# Revit family: 1143210_Oventrop_GmbH___Co__KG_Cocon_QTZ_DN32__PN25__IG_Verschraubung_mit_Messventil
name_source: partatom
category: Rohrzubehör
units: mm (PartAtom-declared; Revit-internal decimal feet)

## family parameters
Arbeitsebenenbasiert = Nein
Beim Laden mit Abzugskörper schneiden = Nein
Bemaßung runder Anschluss = Durchmesser verwenden
Gemeinsam genutzt = Nein
Immer vertikal = Ja
Teiletyp = Normal

## types (1)
- Cocon QTZ Ms-Durchflussregler PN25 (600-4800 l/h), DN 32, kvs 0 m3/h
    Baugruppenkennzeichen = ????
    Beschreibung = OVENTROP-Regulierventil "Cocon QTZ" mit Messventilen, DN32, AG/IG, 600-4800 l/h
    Bestellnummer = 1143210
    Datanorm Nummer = 1143210
    EAN / GTIN = 4026755421644
    Garniturvariante/Einbausituation = mit Messventilen
    Gehäuseanschlussart = Außengewinde/Innengewinde (in Flussrichtung)
    Gehäusebauform = Durchgang
    Gehäusewerkstoff = Messing
    Generiert am = 12.12.2022
    Generiert durch = Rubicon Professional Solutions GmbH
    Hersteller = Oventrop GmbH & Co. KG
    Herstellerkurzname = Oventrop
    Kosten = 0 $
    Modell = Cocon QTZ Ms-Durchflussregler PN25 (600-4800 l/h), DN 32
    Name der Richtlinie = Heizungsarmaturen
    Oberfläche = gebürstet
    Produktgruppe = 7
    Quelle = http://www.vdi3805-portal.de
    Revisionsdatum der VDI-Datei = 29.07.2021
    Stand der Richtlinie = 01.02.2003
    TGA-Nr = 0040270000021000000030000000010050000000000000000100000000?????
    Typenbezeichnung (Name) = Cocon QTZ Ms-Durchflussregler PN25 (600-4800 l/h), DN 32, kvs 0 m3/h
    Typenkommentare = Die Daten geben den Stand des eingeblendeten Datums wieder. Fuer Vollstaendigkeit und Richtigkeit kann keine Gewaehr uebernommen  werden!
    URL = http://www.oventrop.de
    VDI3805-Richtlinienblatt = 2
    Vorgabe-Ansicht = 0 mm  [stored 0 ft]
    Web-Adresse = http://www.vdi3805-portal.de
    WebService = https://www.catalogue.bim4hvac.com:443
    XML = <?xml version="1.0"?>
<pData xmlns="http://www.rubicon-professional.de xmlns:xsi="http://www.w3.org filename="PART02_Oventrop.VDI" shortname="Oventrop" manufacturername="Oventrop GmbH  and  Co. KG" tganr="0040270000021000000030000000010050000000000000000100000000?????" language="de-DE"/><REC010 IDX="010" index="2" content="010;2;200302;Oventrop GmbH  and  Co. KG;20210729;http://www.oventrop.de;Die Daten geben den Stand des eingeblendeten Datums wieder. Fuer Vollstaendigkeit und Richtigkeit kann keine Gewaehr uebernommen  werden!;4026755000009;;;1;20210401;DEU;DE;201110;49;21;"><RECORDS_100><REC100 IDX="100" index="4" content="100;4;4;Absperr- und Regelarmaturen;;;20030317;"><RECORDS_110><REC110 IDX="110" index="27" content="110;27;27;Cocon QTZ Ms-Durchflussregler PN25 (600-4800 l/h);030;3;20180517;;3901;"><RECORDS_200><REC200 IDX="200" index="2" content="200;2;Durchgang;"><RECORDS_250><REC250 IDX="250" index="100" content="250;100;mit Messventilen;"/></RECORDS_250></REC200></RECORDS_200><RECORDS_300><REC300 IDX="300" index="3" content="300;3;Aussengewinde/Innengewinde (in Flussrichtung);"/></RECORDS_300><RECORDS_400><REC400 IDX="400" index="1" content="400;1;Messing;"><RECORDS_450><REC450 IDX="450" index="5" content="450;5;gebuerstet;"/></RECORDS_450></REC400></RECORDS_400><RECORDS_700><REC700 IDX="700" index="1" content="700;1;1;7;32;0;120;16;4000;;;;1;;;;Einstellwert;;;;;;;;;;;;;;;;;;;;;;0;;0;"><RECORDS_710_04><REC71004 IDX="710.04" index="1" content="710.04;1;4.8;;4800;1;320;"/><REC71004 IDX="710.04" index="2" content="710.04;2;3.96;;3960;1;300;"/><REC71004 IDX="710.04" index="3" content="710.04;3;3.12;;3120;1;285;"/><REC71004 IDX="710.04" index="4" content="710.04;4;2.28;;2280;1;265;"/><REC71004 IDX="710.04" index="5" content="710.04;5;1.44;;1440;1;250;"/><REC71004 IDX="710.04" index="6" content="710.04;6;0.6;;600;1;230;"/></RECORDS_710_04><RECORDS_720><REC720 IDX="720" index="1" content="720;1;1143210;;2;100;;3;"/><REC720 IDX="720" index="2" content="720;2;1143270;;2;100;;1;"/><REC720 IDX="720" index="3" content="720;3;1149310;;2;100;;2;"/><REC720 IDX="720" index="11" content="720;11;1143610;;2;101;;3;"/><REC720 IDX="720" index="12" content="720;12;1143670;;2;101;;1;"/><REC720 IDX="720" index="13" content="720;13;1147310;;2;101;;2;"/></RECORDS_720></REC700></RECORDS_700><RECORDS_800><REC800 IDX="800" index="2" content="800;2;0040270000021000000030000000010050000000000000000100000000?????;OVENTROP-Regulierventil  ''Cocon QTZ '' mit Messventilen, DN32, AG/IG, 600-4800 l/h;"><RECORDS_810><REC810 IDX="810" index="1" content="810;1;1143210;1143210;;4026755421644;1143210;;;OVENTROP-Regulierventil  ''Cocon QTZ '' mit Messventilen, DN32, AG/IG, 600-4800 l/h;;;;PCE;;NPL;"/></RECORDS_810></REC800></RECORDS_800></REC110></RECORDS_110></REC100></RECORDS_100><RECORDS_960><REC960 IDX="960" index="2401" content="960;2401;1143210;1A;ovb_w1143104_1;jpg;Fotorealistisches Produktbild in Farbe;"/><REC960 IDX="960" index="2402" content="960;2402;1143210;1A;ovb_w1143210-2;png;Fotorealistisches Produktbild in Farbe;"/><REC960 IDX="960" index="2403" content="960;2403;1143210;1A;ovb_w1143210-1;png;Fotorealistisches Produktbild in Farbe;"/><REC960 IDX="960" index="2404" content="960;2404;1143210;1U;ovu_w1143104_5;jpg;Unvermasste Strichzeichnung;"/><REC960 IDX="960" index="2405" content="960;2405;1143210;1A;ovb_w1143104_3;jpg;Fotorealistisches Produktbild in Farbe;"/></RECORDS_960><RECORDS_970><REC970 IDX="970" index="662" content="970;662;Cocon QTZ DN25 /DN32  NEU (RFER);0;QUAD;-63;-31;-78.5;1;0;0;0;1;0;124;67;140.6;0;0;0;0;0;0;0;0;"><RECORDS_970_02><REC97002 IDX="970.02" index="1" content="970.02;1;G;ZYLI;14.5745;0;53.0265;0.258819;0;0.965926;0;1;0;6;15.8;0;0;0;0;0;0;0;0;12;"/><REC97002 IDX="970.02" index="2" content="970.02;2;G;VKNT;11.0157;0;39.745;0.258819;0;0.965926;0;1;0;13.75;16;6;0;0;0;0;0;0;0;12;"/><REC97002 IDX="970.02" index="3" content="970.02;3;G;KEGL;10.4333;0;37.5717;0.258819;0;0.965926;0;1;0;2.25;12;16;0;0;0;0;0;0;0;1;"/><REC97002 IDX="970.02" index="4" content="970.02;4;G;ZYLI;7.8451;0;27.9124;0.258819;0;0.965926;0;1;0;10;10;0;0;0;0;0;0;0;0;1;"/><REC97002 IDX="970.02" index="5" content="970.02;5;G;KEGL;7.004;0;24.7732;0.258819;0;0.965926;0;1;0;3.25;26;24;0;0;0;0;0;0;0;1;"/><REC97002 IDX="970.02" index="6" content="970.02;6;G;ZYLI;-14.4133;0;-55.1572;0.258819;0;0.965926;0;1;0;82.75;26;0;0;0;0;0;0;0;0;1;80;"/><REC97002 IDX="970.02" index="7" content="970.02;7;G;KEGL;-15.4103;0;-58.8784;0.258819;0;0.965926;0;1;0;3.85245;27.25;25.9999;0;0;0;0;0;0;0;15;"/><REC97002 IDX="970.02" index="8" content="970.02;8;G;QUAD;-13.25;24;-61.25;0.258819;0;0.965926;0;1;0;25.875;11.75;6.5;0;0;0;0;0;0;0;1;"/><REC97002 IDX="970.02" index="9" content="970.02;9;G;KEGL;-16.1221;0;-61.5347;0.258819;0;0.965926;0;1;0;2.75;31;27.25;0;0;0;0;0;0;0;12;"/><REC97002 IDX="970.02" index="10" content="970.02;10;G;ZYLI;-18.0632;0;-68.7791;0.258819;0;0.965926;0;1;0;7.5;31;0;0;0;0;0;0;0;0;12;"/><REC97002 IDX="970.02" index="11" content="970.02;11;G;KEGL;-18.8397;0;-71.6769;0.258819;0;0.965926;0;1;0;3;26;31;0;0;0;0;0;0;0;12;"/><REC97002 IDX="970.02" index="12" content="970.02;12;G;ZYLI;26;3;0;0;1;0;-1;0;0;23;9;0;0;0;0;0;0;0;0;1;80;"/><REC97002 IDX="970.02" index="13" content="970.02;13;G;ZYLI;-17;8;25;0;1;0;-1;0;0;18;9;0;0;0;0;0;0;0;0;1;80;"/><REC97002 IDX="970.02" index="80" content="970.02;80;H;ZYLI;-63;0;0;1;0;0;0;1;0;130;19;0;0;0;0;0;0;0;0;0;"/></RECORDS_970_02><RECORDS_970_03><REC97003 IDX="970.03" index="10" content="970.03;10;G;ROTA;4.399913;0;16.42074198;0.258819;0;0.965926;0;1;0;1;0;0;0;0;0;360;400;0;0;1;1000;"/><REC97003 IDX="970.03" index="15" content="970.03;15;G;ZYLI;26;8;0;0;1;0;-1;0;0;18;9;0;0;0;0;0;0;0;0;1;1000;"/><REC97003 IDX="970.03" index="16" content="970.03;16;G;ROTA;-17;2;25;0;1;0;-1;0;0;1;0;0;0;0;0;360;300;0;0;1;1000;"/><REC97003 IDX="970.03" index="20" content="970.03;20;G;TRAN;-10.35273608;32;-38.63703994;0;-1;0;-0.258819;0;-0.965926;0;0;1;7;150;0;0;0;0;0;1;"/><REC97003 IDX="970.03" index="21" content="970.03;21;G;TRAN;-10.35273608;24;-38.63703994;-0.965926;0;0.258819;0.258819;0;0.965926;0;0;1;8;100;0;0;0;0;0;1;"/><REC97003 IDX="970.03" index="22" content="970.03;22;G;ROTA;-10.35273608;32;-38.63703994;-0.965926;0;0.258819;0.258819;0;0.965926;1;0;0;0;0;0;90;100;0;0;1;"/><REC97003 IDX="970.03" index="23" content="970.03;23;G;TRAN;-10.35273608;32;-38.63703994;-0.965926;0;0.258819;0;1;0;0;0;1;19;100;0;0;0;0;0;1;"/><REC97003 IDX="970.03" index="24" content="970.03;24;G;ROTA;-15.27029549;32;-56.98963129;-0.965926;0;0.258819;0;1;0;1;0;0;0;0;0;90;100;0;0;1;"/><REC97003 IDX="970.03" index="25" content="970.03;25;G;TRAN;-15.27029549;32;-56.98963129;-0.965926;0;0.258819;-0.258819;0;-0.965926;0;0;1;2;100;0;0;0;0;0;1;"/><REC97003 IDX="970.03" index="35" content="970.03;35;G;VKNT;10.61155447;0;39.60296596;0.258819;0;0.965926;0;1;0;14;16;8;0;0;0;0;0;0;0;12;"/><REC97003 IDX="970.03" index="36" content="970.03;36;G;RURO;14.2350121;0;53.12592994;0.258819;0;0.965926;0;1;0;3;6;16;0;0;0;0;0;0;0;12;"/><REC97003 IDX="970.03" index="37" content="970.03;37;G;ZYLI;14.2350121;0;53.12592994;0.258819;0;0.965926;0;1;0;5;13;0;0;0;0;0;0;0;0;12;"/><REC97003 IDX="970.03" index="40" content="970.03;40;G;ZYLI;-12.42328328;0;-46.36444796;-0.258819;0;-0.965926;0;1;0;4;25.9;0;0;0;0;0;0;0;0;4;"/><REC97003 IDX="970.03" index="41" content="970.03;41;G;ZYLI;-13.45855689;0;-50.22815195;-0.258819;0;-0.965926;0;1;0;5;26;0;0;0;0;0;0;0;0;15;"/><REC97003 IDX="970.03" index="42" content="970.03;42;G;VKNT;-20.35558933;24.14814985;-50.96829434;-0.237587;0.969256;0.064001;0.246029;-0.003693;0.969256;5;2;4;0;0;0;0;0;0;0;15;"/><REC97003 IDX="970.03" index="43" content="970.03;43;G;VKNT;-21.5435151;28.99442998;-50.64829235;-0.250075;0.965888;0.067253;0.25896;-0.000206;0.965888;1.5;4;4;0;0;0;0;0;0;0;15;"/><REC97003 IDX="970.03" index="44" content="970.03;44;G;KEGL;-14.7526489;0;-55.05778194;-0.258819;0;-0.965926;0;1;0;4;26.2;27;0;0;0;0;0;0;0;12;"/><REC97003 IDX="970.03" index="45" content="970.03;45;G;KEGL;-15.78792251;0;-58.921486;-0.258819;0;-0.965926;0;1;0;3;27;31;0;0;0;0;0;0;0;12;"/><REC97003 IDX="970.03" index="46" content="970.03;46;G;VKNT;-16.56437772;0;-61.81926393;-0.258819;0;-0.965926;0;1;0;7;31;70;0;0;0;0;0;0;0;12;"/><REC97003 IDX="970.03" index="47" content="970.03;47;G;KEGL;-18.37610653;0;-68.58074592;-0.258819;0;-0.965926;0;1;0;3;31;26;0;0;0;0;0;0;0;12;"/><REC97003 IDX="970.03" index="48" content="970.03;48;G;ROTA;-14.7526489;0;-55.05778194;-0.791292;0.573513;0.211989;-0.258787;-0.000016;-0.965934;0;1;0;0;0;0;45;200;0;0;12;"/><REC97003 IDX="970.03" index="100" content="970.03;100;D;STRE;0;0;0;1;0;0;0;1;0;101;-3.5;0;3.5;0;0;0;0;0;0;0;"/><REC97003 IDX="970.03" index="101" content="970.03;101;D;BOGN;0;0;0;1;0;0;0;1;0;100;3.5;0;-3.5;0;3.5;0;0;0;0;0;"/><REC97003 IDX="970.03" index="150" content="970.03;150;D;STRE;0;0;-3.5;1;0;0;0;1;0;151;0;0;0;19;0;0;0;0;0;0;"/><REC97003 IDX="970.03" index="151" content="970.03;151;D;STRE;0;0;-3.5;1;0;0;0;1;0;152;0;19;2;19;0;0;0;0;0;0;"/><REC97003 IDX="970.03" index="152" content="970.03;152;D;STRE;0;0;-3.5;1;0;0;0;1;0;153;2;19;2;15;0;0;0;0;0;0;"/><REC97003 IDX="970.03" index="153" content="970.03;153;D;STRE;0;0;-3.5;1;0;0;0;1;0;154;2;15;5;12;0;0;0;0;0;0;"/><REC97003 IDX="970.03" index="154" content="970.03;154;D;STRE;0;0;-3.5;1;0;0;0;1;0;155;5;12;5;8;0;0;0;0;0;0;"/><REC97003 IDX="970.03" index="155" content="970.03;155;D;STRE;0;0;-3.5;1;0;0;0;1;0;156;5;8;8;8;0;0;0;0;0;0;"/><REC97003 IDX="970.03" index="156" content="970.03;156;D;STRE;0;0;-3.5;1;0;0;0;1;0;157;8;8;8;0;0;0;0;0;0;0;"/><REC97003 IDX="970.03" index="157" content="970.03;157;D;STRE;0;0;-3.5;1;0;0;0;1;0;150;8;0;0;0;0;0;0;0;0;0;"/><REC97003 IDX="970.03" index="200" content="970.03;200;D;STRE;0;0;0;1;0;0;0;1;0;201;0;0;28;0;0;0;0;0;0;0;"/><REC97003 IDX="970.03" index="201" content="970.03;201;D;STRE;0;0;0;1;0;0;0;1;0;202;28;0;31;3;0;0;0;0;0;0;"/><REC97003 IDX="970.03" index="202" content="970.03;202;D;STRE;0;0;0;1;0;0;0;1;0;203;31;3;31;7;0;0;0;0;0;0;"/><REC97003 IDX="970.03" index="203" content="970.03;203;D;STRE;0;0;0;1;0;0;0;1;0;204;31;7;0;7;0;0;0;0;0;0;"/><REC97003 IDX="970.03" index="204" content="970.03;204;D;STRE;0;0;0;1;0;0;0;1;0;200;0;7;0;0;0;0;0;0;0;0;"/><REC97003 IDX="970.03" index="300" content="970.03;300;D;STRE;0;0;0;1;0;0;0;1;0;301;24;9;0;9;0;0;0;0;0;0;"/><REC97003 IDX="970.03" index="301" content="970.03;301;D;BOGN;0;0;0;1;0;0;0;1;0;302;0;9;-5;0;10;4.99433749;0.33647917;0;0;0;"/><REC97003 IDX="970.03" index="302" content="970.03;302;D;STRE;0;0;0;1;0;0;0;1;0;303;-5;0;24;0;0;0;0;0;0;0;"/><REC97003 IDX="970.03" index="303" content="970.03;303;D;STRE;0;0;0;1;0;0;0;1;0;300;24;0;24;9;0;0;0;0;0;0;"/><REC97003 IDX="970.03" index="400" content="970.03;400;D;STRE;0;0;0;1;0;0;0;1;0;401;-65;26;9;26;0;0;0;0;0;0;"/><REC97003 IDX="970.03" index="401" content="970.03;401;D;BOGN;0;0;0;1;0;0;0;1;0;402;12;23;9;26;3;9;23;0;0;0;"/><REC97003 IDX="970.03" index="402" content="970.03;402;D;STRE;0;0;0;1;0;0;0;1;0;403;12;23;12;12;0;0;0;0;0;0;"/><REC97003 IDX="970.03" index="403" content="970.03;403;D;BOGN;0;0;0;1;0;0;0;1;0;404;12;12;14;10;2;14;12;0;0;0;"/><REC97003 IDX="970.03" index="404" content="970.03;404;D;STRE;0;0;0;1;0;0;0;1;0;405;14;10;21;10;0;0;0;0;0;0;"/><REC97003 IDX="970.03" index="405" content="970.03;405;D;BOGN;0;0;0;1;0;0;0;1;0;406;21;10;22;11;2;20.17712434;11.82287566;0;0;0;"/><REC97003 IDX="970.03" index="406" content="970.03;406;D;STRE;0;0;0;1;0;0;0;1;0;407;22;11;23;15;0;0;0;0;0;0;"/><REC97003 IDX="970.03" index="407" content="970.03;407;D;BOGN;0;0;0;1;0;0;0;1;0;408;24;16;23;15;1;24;15;0;0;0;"/><REC97003 IDX="970.03" index="408" content="970.03;408;D;STRE;0;0;0;1;0;0;0;1;0;409;24;16;24;0;0;0;0;0;0;0;"/><REC97003 IDX="970.03" index="409" content="970.03;409;D;STRE;0;0;0;1;0;0;0;1;0;410;24;0;-65;0;0;0;0;0;0;0;"/><REC97003 IDX="970.03" index="410" content="970.03;410;D;STRE;0;0;0;1;0;0;0;1;0;400;-65;0;-65;26;0;0;0;0;0;0;"/><REC97003 IDX="970.03" index="1000" content="970.03;1000;H;ZYLI;-50;0;0;1;0;0;0;1;0;100;18;0;0;0;0;0;0;0;0;0;"/></RECORDS_970_03><RECORDS_970_04><REC97004 IDX="970.04" index="1" content="970.04;1;0.8078;0.6235;0;1;0.9059;0.7765;0.0471;1;0.9294;0.7922;0.0118;1;60;0;0;0;1;"/><REC97004 IDX="970.04" index="4" content="970.04;4;0.8078;0.6235;0;1;0.8;0.6;0.1;1;1;1;1;1;48;0;0;0;1;"/><REC97004 IDX="970.04" index="12" content="970.04;12;0.4353;0.4353;0.4353;1;0.2471;0.2471;0.2471;1;0.6235;0.6235;0.6235;1;50;0;0;0;1;"/><REC97004 IDX="970.04" index="15" content="970.04;15;0.8;0;0;1;1;0;0.2471;1;1;0.4157;0.4157;1;80;0;0;0;1;"/></RECORDS_970_04></REC970><REC970 IDX="970" index="673" content="970;673;CoConDN32 Verschrbg IG (RFER);0;QUAD;-102;-26;-30.0222;1;0;0;0;1;0;165;52;60.0444;0;0;0;0;0;0;0;0;"><RECORDS_970_02><REC97002 IDX="970.02" index="1" content="970.02;1;H;ZYLI;-102;0;0;1;0;0;0;0;1;172.5;17.95;0;0;0;0;0;0;0;0;0;"/><REC97002 IDX="970.02" index="2" content="970.02;2;G;VKNT;-69;0;0;1;0;0;0;0;1;20;26;6;0;0;0;0;0;0;0;1;1;"/><REC97002 IDX="970.02" index="3" content="970.02;3;G;VKNT;39;0;0;1;0;0;0;0;1;24;24;6;0;0;0;0;0;0;0;1;1;"/><REC97002 IDX="970.02" index="4" content="970.02;4;G;ROTA;-102;0;-22;1;0;0;0;0;1;1;0;0;0;22;0;360;100;0;0;1;"/><REC97002 IDX="970.02" index="100" content="970.02;100;D;STRE;0;0;0;1;0;0;0;1;0;101;61;0;61;2;0;0;0;0;0;0;"/><REC97002 IDX="970.02" index="101" content="970.02;101;D;STRE;0;0;0;1;0;0;0;1;0;102;139;2.00001;61;2;0;0;0;0;0;0;"/><REC97002 IDX="970.02" index="102" content="970.02;102;D;STRE;0;0;0;1;0;0;0;1;0;103;141;0;139;2.00001;0;0;0;0;0;0;"/><REC97002 IDX="970.02" index="103" content="970.02;103;D;STRE;0;0;0;1;0;0;0;1;0;104;141;0;141;4;0;0;0;0;0;0;"/><REC97002 IDX="970.02" index="104" content="970.02;104;D;STRE;0;0;0;1;0;0;0;1;0;105;137;4;141;4;0;0;0;0;0;0;"/><REC97002 IDX="970.02" index="105" content="970.02;105;D;STRE;0;0;0;1;0;0;0;1;0;106;137;4.05;137;4;0;0;0;0;0;0;"/><REC97002 IDX="970.02" index="106" content="970.02;106;D;STRE;0;0;0;1;0;0;0;1;0;107;137;4.05;0;4.05;0;0;0;0;0;0;"/><REC97002 IDX="970.02" index="107" content="970.02;107;D;STRE;0;0;0;1;0;0;0;1;0;108;0;2.8;0;4.05;0;0;0;0;0;0;"/><REC97002 IDX="970.02" index="108" content="970.02;108;D;STRE;0;0;0;1;0;0;0;1;0;109;0;2.8;1;1.8;0;0;0;0;0;0;"/><REC97002 IDX="970.02" index="109" content="970.02;109;D;STRE;0;0;0;1;0;0;0;1;0;110;1;1.8;19;0.700001;0;0;0;0;0;0;"/><REC97002 IDX="970.02" index="110" content="970.02;110;D;STRE;0;0;0;1;0;0;0;1;0;111;19;0.700001;36.25;0.700005;0;0;0;0;0;0;"/><REC97002 IDX="970.02" index="111" content="970.02;111;D;STRE;0;0;0;1;0;0;0;1;0;112;36.25;0.700005;53;0;0;0;0;0;0;0;"/><REC97002 IDX="970.02" index="112" content="970.02;112;D;STRE;0;0;0;1;0;0;0;1;0;100;53;0;61;0;0;0;0;0;0;0;"/></RECORDS_970_02><RECORDS_970_03><REC97003 IDX="970.03" index="1" content="970.03;1;G;ROTA;-68;21.2;0;-1;0;0;0;1;0;1;0;0;0;-21.2;0;360;90;0;0;4;"/><REC97003 IDX="970.03" index="2" content="970.03;2;G;VKNT;-69;0;0;1;0;0;0;0.866025;0.5;20;26;6;0;0;0;0;0;0;0;1;1000;"/><REC97003 IDX="970.03" index="3" content="970.03;3;G;RURO;-49;0;0;1;0;0;0;1;0;3;8;25;0;0;0;0;0;0;0;1;"/><REC97003 IDX="970.03" index="4" content="970.03;4;G;RURO;-62;0;0;1;0;0;0;1;0;2;50;21.9;0;0;0;0;0;0;0;1;"/><REC97003 IDX="970.03" index="7" content="970.03;7;G;VKNT;63;0;0;-1;0;0;0;0.866025;-0.5;24;24;6;0;0;0;0;0;0;0;1;1010;"/><REC97003 IDX="970.03" index="8" content="970.03;8;G;RURR;39;0;0;-1;0;0;0;1;0;2;4;24;20;20;0;0;0;0;0;1;"/><REC97003 IDX="970.03" index="9" content="970.03;9;G;RURO;35;0;0;-1;0;0;0;1;0;2;19;20;0;0;0;0;0;0;0;1;"/><REC97003 IDX="970.03" index="90" content="970.03;90;D;STRE;0;0;0;1;0;0;0;1;0;91;0;0;15;0;0;0;0;0;0;0;"/><REC97003 IDX="970.03" index="91" content="970.03;91;D;STRE;0;0;0;1;0;0;0;1;0;92;15;0;33;-1;0;0;0;0;0;0;"/><REC97003 IDX="970.03" index="92" content="970.03;92;D;STRE;0;0;0;1;0;0;0;1;0;93;33;-1;34;-2;0;0;0;0;0;0;"/><REC97003 IDX="970.03" index="93" content="970.03;93;D;STRE;0;0;0;1;0;0;0;1;0;94;34;-2;34;-3;0;0;0;0;0;0;"/><REC97003 IDX="970.03" index="94" content="970.03;94;D;STRE;0;0;0;1;0;0;0;1;0;95;34;-3;0;-3;0;0;0;0;0;0;"/><REC97003 IDX="970.03" index="95" content="970.03;95;D;STRE;0;0;0;1;0;0;0;1;0;90;0;-3;0;0;0;0;0;0;0;0;"/><REC97003 IDX="970.03" index="1000" content="970.03;1000;H;ZYLI;-70;0;0;1;0;0;0;1;0;30;18;0;0;0;0;0;0;0;0;0;"/><REC97003 IDX="970.03" index="1010" content="970.03;1010;H;ZYLI;35;0;0;1;0;0;0;1;0;30;21;0;0;0;0;0;0;0;0;0;"/></RECORDS_970_03><RECORDS_970_04><REC97004 IDX="970.04" index="1" content="970.04;1;0.8078;0.6235;0;1;0.9059;0.7765;0.0471;1;0.9294;0.7922;0.0118;1;60;0;0;0;1;"/><REC97004 IDX="970.04" index="4" content="970.04;4;0.8078;0.6235;0;1;0.8;0.6;0.1;1;1;1;1;1;48;0;0;0;1;"/></RECORDS_970_04></REC970><REC970 IDX="970" index="154" content="970;154;Messfuehler, classic, Messing NEU blau (REFR);0;QUAD;-9.2376;0;-14.5;1;0;0;0;1;0;18.4752;38.05;23.5;0;0;0;0;0;0;0;0;"><RECORDS_970_02><REC97002 IDX="970.02" index="1" content="970.02;1;D;STRE;0;0;0;1;0;0;0;1;0;2;1.25;3.5;1.25;1;0;0;0;0;0;0;"/><REC97002 IDX="970.02" index="2" content="970.02;2;D;STRE;0;0;0;1;0;0;0;1;0;3;1.25;1;0;0;0;0;0;0;0;0;"/><REC97002 IDX="970.02" index="3" content="970.02;3;D;STRE;0;0;0;1;0;0;0;1;0;4;0;0;8.75;0;0;0;0;0;0;0;"/><REC97002 IDX="970.02" index="4" content="970.02;4;D;STRE;0;0;0;1;0;0;0;1;0;5;8.75;38.05;8.75;0;0;0;0;0;0;0;"/><REC97002 IDX="970.02" index="5" content="970.02;5;D;STRE;0;0;0;1;0;0;0;1;0;6;8.75;38.05;4.5;38.05;0;0;0;0;0;0;"/><REC97002 IDX="970.02" index="6" content="970.02;6;D;STRE;0;0;0;1;0;0;0;1;0;7;4.5;38.05;3.5;37.25;0;0;0;0;0;0;"/><REC97002 IDX="970.02" index="7" content="970.02;7;D;STRE;0;0;0;1;0;0;0;1;0;8;3.5;37.25;3.5;32.75;0;0;0;0;0;0;"/><REC97002 IDX="970.02" index="8" content="970.02;8;D;STRE;0;0;0;1;0;0;0;1;0;9;3.5;32.75;4.25;32.75;0;0;0;0;0;0;"/><REC97002 IDX="970.02" index="9" content="970.02;9;D;STRE;0;0;0;1;0;0;0;1;0;10;4.25;32.75;4.25;30.75;0;0;0;0;0;0;"/><REC97002 IDX="970.02" index="10" content="970.02;10;D;STRE;0;0;0;1;0;0;0;1;0;11;2.25;30.75;4.25;30.75;0;0;0;0;0;0;"/><REC97002 IDX="970.02" index="11" content="970.02;11;D;STRE;0;0;0;1;0;0;0;1;0;12;2.25;30.75;2.25;29.75;0;0;0;0;0;0;"/><REC97002 IDX="970.02" index="12" content="970.02;12;D;STRE;0;0;0;1;0;0;0;1;0;13;2.25;29.75;4.75;29.75;0;0;0;0;0;0;"/><REC97002 IDX="970.02" index="13" content="970.02;13;D;STRE;0;0;0;1;0;0;0;1;0;14;4.75;29.75;4.75;27.75;0;0;0;0;0;0;"/><REC97002 IDX="970.02" index="14" content="970.02;14;D;STRE;0;0;0;1;0;0;0;1;0;15;4.75;27.75;1.5;27.75;0;0;0;0;0;0;"/><REC97002 IDX="970.02" index="15" content="970.02;15;D;STRE;0;0;0;1;0;0;0;1;0;16;1.5;27.75;0.75;27;0;0;0;0;0;0;"/><REC97002 IDX="970.02" index="16" content="970.02;16;D;STRE;0;0;0;1;0;0;0;1;0;17;0.75;27;0.75;14.5;0;0;0;0;0;0;"/><REC97002 IDX="970.02" index="17" content="970.02;17;D;STRE;0;0;0;1;0;0;0;1;0;18;0.75;14.5;4.13;14.5;0;0;0;0;0;0;"/><REC97002 IDX="970.02" index="18" content="970.02;18;D;STRE;0;0;0;1;0;0;0;1;0;19;4.13;14.5;4.13;3.5;0;0;0;0;0;0;"/><REC97002 IDX="970.02" index="19" content="970.02;19;D;STRE;0;0;0;1;0;0;0;1;0;1;4.13;3.5;1.25;3.5;0;0;0;0;0;0;"/><REC97002 IDX="970.02" index="20" content="970.02;20;G;ROTA;-8.7496;0;0;1;0;0;0;1;0;0;1;0;8.7496;0;0;360;1;0;0;1;"/><REC97002 IDX="970.02" index="21" content="970.02;21;G;VKNT;0;3.5;0;0;1;0;-1;0;0;11;8;6;0;0;0;0;0;0;0;1;"/><REC97002 IDX="970.02" index="22" content="970.02;22;D;BOGN;0;0;0;1;0;0;0;1;0;23;13;6.43774;5;6.43774;9;9;14.5;0;0;0;"/><REC97002 IDX="970.02" index="23" content="970.02;23;D;STRE;0;0;0;1;0;0;0;1;0;24;5;6.43774;5;0;0;0;0;0;0;0;"/><REC97002 IDX="970.02" index="24" content="970.02;24;D;STRE;0;0;0;1;0;0;0;1;0;25;5;0;13;0;0;0;0;0;0;0;"/><REC97002 IDX="970.02" index="25" content="970.02;25;D;STRE;0;0;0;1;0;0;0;1;0;22;13;6.43774;13;0;0;0;0;0;0;0;"/><REC97002 IDX="970.02" index="26" content="970.02;26;G;TRAN;-9;29.75;-14.5;1;0;0;0;0;1;0;0;1;2;22;0;0;0;0;0;22;"/></RECORDS_970_02><RECORDS_970_03><REC97003 IDX="970.03" index="1" content="970.03;1;D;BOGN;0;0;0;1;0;0;0;1;0;2;13;6.43774;5;6.43774;9;9;14.5;0;0;0;"/><REC97003 IDX="970.03" index="2" content="970.03;2;D;STRE;0;0;0;1;0;0;0;1;0;3;5;6.43774;5;0;0;0;0;0;0;0;"/><REC97003 IDX="970.03" index="3" content="970.03;3;D;STRE;0;0;0;1;0;0;0;1;0;4;5;0;13;0;0;0;0;0;0;0;"/><REC97003 IDX="970.03" index="4" content="970.03;4;D;STRE;0;0;0;1;0;0;0;1;0;1;13;6.43774;13;0;0;0;0;0;0;0;"/><REC97003 IDX="970.03" index="5" content="970.03;5;G;TRAN;-9;29.75;-14.5;1;0;0;0;0;1;0;0;1;2;1;0;0;0;0;0;22;"/><REC97003 IDX="970.03" index="6" content="970.03;6;G;ZYLI;0;27.75;0;0;1;0;-1;0;0;2;4.5;0;0;0;0;0;0;0;0;4;"/><REC97003 IDX="970.03" index="7" content="970.03;7;G;KEGL;0;37.25;0;0;1;0;-1;0;0;0.8;6;5;0;0;0;0;0;0;0;4;"/><REC97003 IDX="970.03" index="8" content="970.03;8;G;VKNT;0;32.75;0;0;1;0;-1;0;0;4.5;6;24;0;0;0;0;0;0;0;4;"/><REC97003 IDX="970.03" index="9" content="970.03;9;G;ZYLI;0;30.75;0;0;1;0;-1;0;0;2;4.5;0;0;0;0;0;0;0;0;4;"/><REC97003 IDX="970.03" index="10" content="970.03;10;G;ZYLI;0;29.75;0;0;1;0;-1;0;0;1;6.5;0;0;0;0;0;0;0;0;4;"/><REC97003 IDX="970.03" index="11" content="970.03;11;G;KEGL;0;27;0;0;1;0;-1;0;0;0.75;8.75;8;0;0;0;0;0;0;0;4;"/><REC97003 IDX="970.03" index="12" content="970.03;12;G;ZYLI;0;14.5;0;0;1;0;-1;0;0;12.5;8.75;0;0;0;0;0;0;0;0;4;"/><REC97003 IDX="970.03" index="13" content="970.03;13;G;VKNT;0;3.5;0;0;1;0;-1;0;0;11;8;6;0;0;0;0;0;0;0;4;"/><REC97003 IDX="970.03" index="14" content="970.03;14;G;ZYLI;0;1;0;0;1;0;-1;0;0;3;8.25;0;0;0;0;0;0;0;0;4;"/><REC97003 IDX="970.03" index="15" content="970.03;15;G;KEGL;0;0;0;0;1;0;-1;0;0;1;8.75;8;0;0;0;0;0;0;0;4;"/></RECORDS_970_03><RECORDS_970_04><REC97004 IDX="970.04" index="1" content="970.04;1;0.8078;0.6235;0;1;0.9059;0.7765;0.0471;1;0.9294;0.7922;0.0118;1;60;0;0;0;1;"/><REC97004 IDX="970.04" index="4" content="970.04;4;0.8078;0.6235;0;1;0.8;0.6;0.1;1;1;1;1;1;48;0;0;0;1;"/><REC97004 IDX="970.04" index="22" content="970.04;22;0;0.502;1;1;0.4;0.7;0.7;1;0.3;0.3;0.3;1;16;0;0;0;1;"/></RECORDS_970_04></REC970><REC970 IDX="970" index="153" content="970;153;Messfuehler, classic, Messing NEU rot (REFR);0;QUAD;-9.2376;0;-14.5;1;0;0;0;1;0;18.4752;38.05;23.5;0;0;0;0;0;0;0;0;"><RECORDS_970_02><REC97002 IDX="970.02" index="1" content="970.02;1;D;STRE;0;0;0;1;0;0;0;1;0;2;1.25;3.5;1.25;1;0;0;0;0;0;0;"/><REC97002 IDX="970.02" index="2" content="970.02;2;D;STRE;0;0;0;1;0;0;0;1;0;3;1.25;1;0;0;0;0;0;0;0;0;"/><REC97002 IDX="970.02" index="3" content="970.02;3;D;STRE;0;0;0;1;0;0;0;1;0;4;0;0;8.75;0;0;0;0;0;0;0;"/><REC97002 IDX="970.02" index="4" content="970.02;4;D;STRE;0;0;0;1;0;0;0;1;0;5;8.75;38.05;8.75;0;0;0;0;0;0;0;"/><REC97002 IDX="970.02" index="5" content="970.02;5;D;STRE;0;0;0;1;0;0;0;1;0;6;8.75;38.05;4.5;38.05;0;0;0;0;0;0;"/><REC97002 IDX="970.02" index="6" content="970.02;6;D;STRE;0;0;0;1;0;0;0;1;0;7;4.5;38.05;3.5;37.25;0;0;0;0;0;0;"/><REC97002 IDX="970.02" index="7" content="970.02;7;D;STRE;0;0;0;1;0;0;0;1;0;8;3.5;37.25;3.5;32.75;0;0;0;0;0;0;"/><REC97002 IDX="970.02" index="8" content="970.02;8;D;STRE;0;0;0;1;0;0;0;1;0;9;3.5;32.75;4.25;32.75;0;0;0;0;0;0;"/><REC97002 IDX="970.02" index="9" content="970.02;9;D;STRE;0;0;0;1;0;0;0;1;0;10;4.25;32.75;4.25;30.75;0;0;0;0;0;0;"/><REC97002 IDX="970.02" index="10" content="970.02;10;D;STRE;0;0;0;1;0;0;0;1;0;11;2.25;30.75;4.25;30.75;0;0;0;0;0;0;"/><REC97002 IDX="970.02" index="11" content="970.02;11;D;STRE;0;0;0;1;0;0;0;1;0;12;2.25;30.75;2.25;29.75;0;0;0;0;0;0;"/><REC97002 IDX="970.02" index="12" content="970.02;12;D;STRE;0;0;0;1;0;0;0;1;0;13;2.25;29.75;4.75;29.75;0;0;0;0;0;0;"/><REC97002 IDX="970.02" index="13" content="970.02;13;D;STRE;0;0;0;1;0;0;0;1;0;14;4.75;29.75;4.75;27.75;0;0;0;0;0;0;"/><REC97002 IDX="970.02" index="14" content="970.02;14;D;STRE;0;0;0;1;0;0;0;1;0;15;4.75;27.75;1.5;27.75;0;0;0;0;0;0;"/><REC97002 IDX="970.02" index="15" content="970.02;15;D;STRE;0;0;0;1;0;0;0;1;0;16;1.5;27.75;0.75;27;0;0;0;0;0;0;"/><REC97002 IDX="970.02" index="16" content="970.02;16;D;STRE;0;0;0;1;0;0;0;1;0;17;0.75;27;0.75;14.5;0;0;0;0;0;0;"/><REC97002 IDX="970.02" index="17" content="970.02;17;D;STRE;0;0;0;1;0;0;0;1;0;18;0.75;14.5;4.13;14.5;0;0;0;0;0;0;"/><REC97002 IDX="970.02" index="18" content="970.02;18;D;STRE;0;0;0;1;0;0;0;1;0;19;4.13;14.5;4.13;3.5;0;0;0;0;0;0;"/><REC97002 IDX="970.02" index="19" content="970.02;19;D;STRE;0;0;0;1;0;0;0;1;0;1;4.13;3.5;1.25;3.5;0;0;0;0;0;0;"/><REC97002 IDX="970.02" index="20" content="970.02;20;G;ROTA;-8.7496;0;0;1;0;0;0;1;0;0;1;0;8.7496;0;0;360;1;0;0;1;"/><REC97002 IDX="970.02" index="21" content="970.02;21;G;VKNT;0;3.5;0;0;1;0;-1;0;0;11;8;6;0;0;0;0;0;0;0;1;"/><REC97002 IDX="970.02" index="22" content="970.02;22;D;BOGN;0;0;0;1;0;0;0;1;0;23;13;6.43774;5;6.43774;9;9;14.5;0;0;0;"/><REC97002 IDX="970.02" index="23" content="970.02;23;D;STRE;0;0;0;1;0;0;0;1;0;24;5;6.43774;5;0;0;0;0;0;0;0;"/><REC97002 IDX="970.02" index="24" content="970.02;24;D;STRE;0;0;0;1;0;0;0;1;0;25;5;0;13;0;0;0;0;0;0;0;"/><REC97002 IDX="970.02" index="25" content="970.02;25;D;STRE;0;0;0;1;0;0;0;1;0;22;13;6.43774;13;0;0;0;0;0;0;0;"/><REC97002 IDX="970.02" index="26" content="970.02;26;G;TRAN;-9;29.75;-14.5;1;0;0;0;0;1;0;0;1;2;22;0;0;0;0;0;15;"/></RECORDS_970_02><RECORDS_970_03><REC97003 IDX="970.03" index="1" content="970.03;1;D;BOGN;0;0;0;1;0;0;0;1;0;2;13;6.43774;5;6.43774;9;9;14.5;0;0;0;"/><REC97003 IDX="970.03" index="2" content="970.03;2;D;STRE;0;0;0;1;0;0;0;1;0;3;5;6.43774;5;0;0;0;0;0;0;0;"/><REC97003 IDX="970.03" index="3" content="970.03;3;D;STRE;0;0;0;1;0;0;0;1;0;4;5;0;13;0;0;0;0;0;0;0;"/><REC97003 IDX="970.03" index="4" content="970.03;4;D;STRE;0;0;0;1;0;0;0;1;0;1;13;6.43774;13;0;0;0;0;0;0;0;"/><REC97003 IDX="970.03" index="5" content="970.03;5;G;TRAN;-9;29.75;-14.5;1;0;0;0;0;1;0;0;1;2;1;0;0;0;0;0;15;"/><REC97003 IDX="970.03" index="6" content="970.03;6;G;ZYLI;0;27.75;0;0;1;0;-1;0;0;2;4.5;0;0;0;0;0;0;0;0;4;"/><REC97003 IDX="970.03" index="7" content="970.03;7;G;KEGL;0;37.25;0;0;1;0;-1;0;0;0.8;6;5;0;0;0;0;0;0;0;4;"/><REC97003 IDX="970.03" index="8" content="970.03;8;G;VKNT;0;32.75;0;0;1;0;-1;0;0;4.5;6;24;0;0;0;0;0;0;0;4;"/><REC97003 IDX="970.03" index="9" content="970.03;9;G;ZYLI;0;30.75;0;0;1;0;-1;0;0;2;4.5;0;0;0;0;0;0;0;0;4;"/><REC97003 IDX="970.03" index="10" content="970.03;10;G;ZYLI;0;29.75;0;0;1;0;-1;0;0;1;6.5;0;0;0;0;0;0;0;0;4;"/><REC97003 IDX="970.03" index="11" content="970.03;11;G;KEGL;0;27;0;0;1;0;-1;0;0;0.75;8.75;8;0;0;0;0;0;0;0;4;"/><REC97003 IDX="970.03" index="12" content="970.03;12;G;ZYLI;0;14.5;0;0;1;0;-1;0;0;12.5;8.75;0;0;0;0;0;0;0;0;4;"/><REC97003 IDX="970.03" index="13" content="970.03;13;G;VKNT;0;3.5;0;0;1;0;-1;0;0;11;8;6;0;0;0;0;0;0;0;4;"/><REC97003 IDX="970.03" index="14" content="970.03;14;G;ZYLI;0;1;0;0;1;0;-1;0;0;3;8.25;0;0;0;0;0;0;0;0;4;"/><REC97003 IDX="970.03" index="15" content="970.03;15;G;KEGL;0;0;0;0;1;0;-1;0;0;1;8.75;8;0;0;0;0;0;0;0;4;"/></RECORDS_970_03><RECORDS_970_04><REC97004 IDX="970.04" index="1" content="970.04;1;0.8078;0.6235;0;1;0.9059;0.7765;0.0471;1;0.9294;0.7922;0.0118;1;60;0;0;0;1;"/><REC97004 IDX="970.04" index="4" content="970.04;4;0.8078;0.6235;0;1;0.8;0.6;0.1;1;1;1;1;1;48;0;0;0;1;"/><REC97004 IDX="970.04" index="15" content="970.04;15;0.8;0;0;1;1;0;0.2471;1;1;0.4157;0.4157;1;80;0;0;0;1;"/></RECORDS_970_04></REC970><REC970 IDX="970" index="1143210" content="970;1143210;Cocon QTZ DN32, PN25, IG/Verschraubung mit Messventil;0;QUAD;-102;-40;-79;1;0;0;0;1;0;165;115;145;0;0;0;0;0;0;0;0;"><RECORDS_970_01><REC97001 IDX="970.01" index="1" content="970.01;1;1;E;Vorlauf;NIPP;10226;DN;32;0;20;-102;0;0;-1;0;0;0;1;0;0;0;0;0;0;0;"/><REC97001 IDX="970.01" index="2" content="970.01;2;2;A;Ruecklauf;MUFF;228T1;DN;32;0;20;63;0;0;1;0;0;0;1;0;0;0;0;0;0;0;"/></RECORDS_970_01><RECORDS_970_02><REC97002 IDX="970.02" index="10" content="970.02;10;G;RFER;0;0;0;1;0;0;0;1;0;0;0;0;662;0;0;0;0;0;0;0;"/><REC97002 IDX="970.02" index="11" content="970.02;11;G;RFER;0;0;0;1;0;0;0;1;0;0;0;0;673;0;0;0;0;0;0;0;"/><REC97002 IDX="970.02" index="50" content="970.02;50;G;RFER;26;26;0;1;0;0;0;1;0;0;0;0;154;0;0;0;0;0;0;0;"/><REC97002 IDX="970.02" index="51" content="970.02;51;G;RFER;-17;26;25;1;0;0;0;1;0;0;0;0;153;0;0;0;0;0;0;0;"/></RECORDS_970_02><RECORDS_970_03><REC97003 IDX="970.03" index="10" content="970.03;10;G;RFER;0;0;0;1;0;0;0;1;0;0;0;0;662;0;0;0;0;0;0;0;"/><REC97003 IDX="970.03" index="11" content="970.03;11;G;RFER;0;0;0;1;0;0;0;1;0;0;0;0;673;0;0;0;0;0;0;0;"/><REC97003 IDX="970.03" index="50" content="970.03;50;G;RFER;26;26;0;1;0;0;0;1;0;0;0;0;154;0;0;0;0;0;0;0;"/><REC97003 IDX="970.03" index="51" content="970.03;51;G;RFER;-17;26;25;1;0;0;0;1;0;0;0;0;153;0;0;0;0;0;0;0;"/></RECORDS_970_03></REC970></RECORDS_970></REC010></pData>

note: [stored X ft] marks values corroborated as IEEE doubles in the binary element streams (Revit-internal decimal feet)

## geometry (parser evidence)
native form markers: Sweep x2
no freeform markers — native parametric forms only
